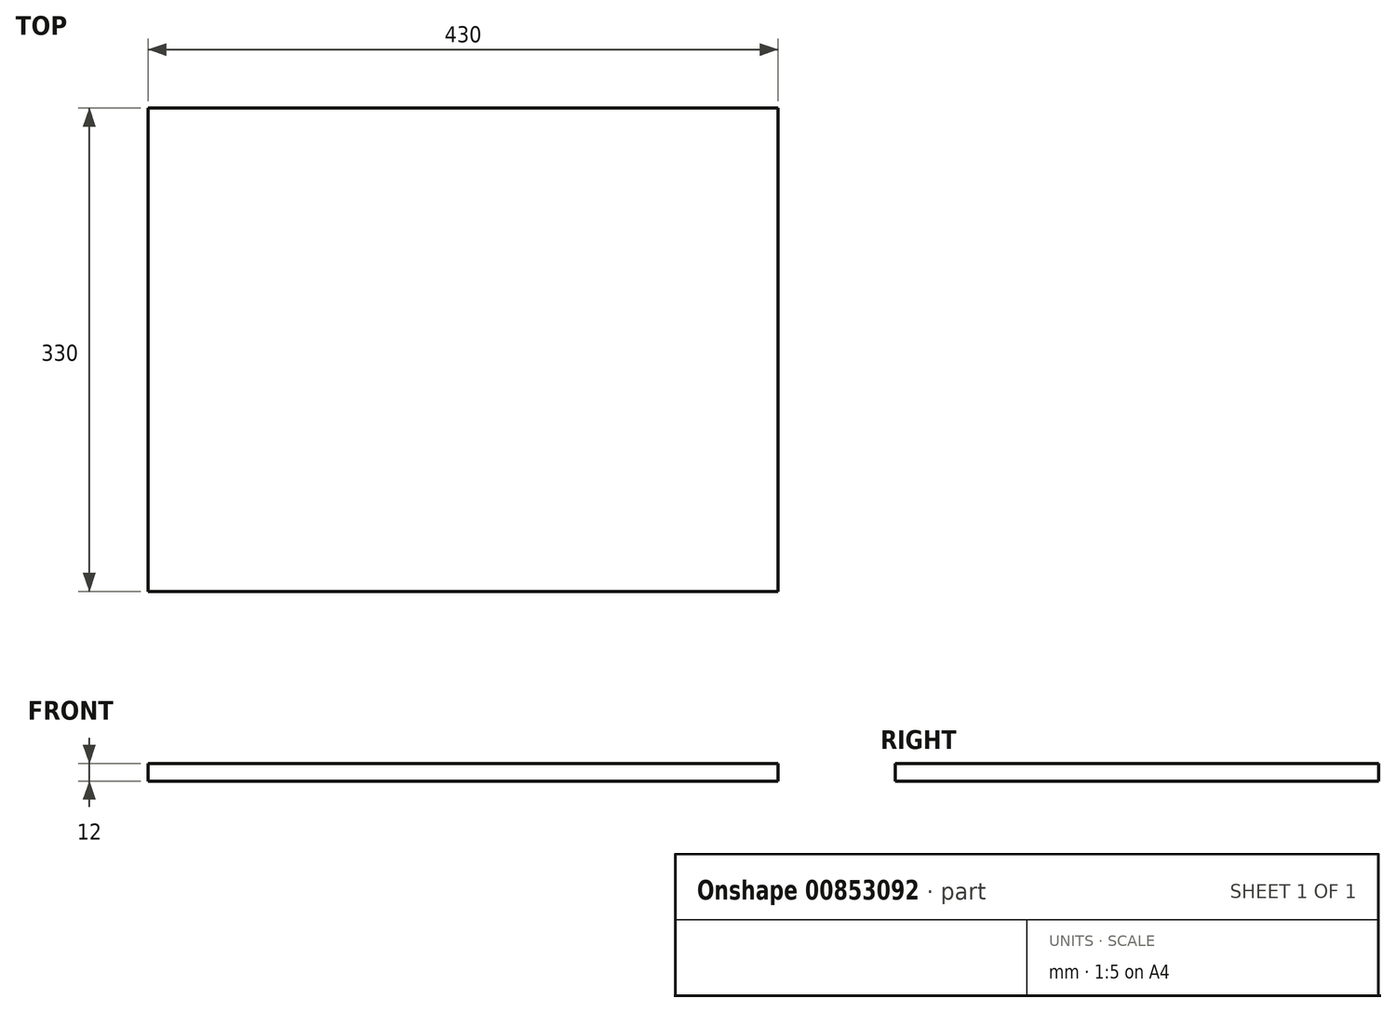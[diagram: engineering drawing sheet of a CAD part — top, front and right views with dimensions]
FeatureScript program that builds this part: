
annotation { "Feature Type Name" : "Feature", "Feature Type Description" : "" }
export const myFeature = defineFeature(function(context is Context, id is Id, definition is map)
    precondition{}
    {
        {
            var Q0;
            Q0=qCreatedBy(makeId("Top.planeOp"),FACE);
            var sketch = newSketch(context, id + "F0", { "sketchPlane" : qUnion([Q0])});
            skLineSegment(sketch, "E0.bottom", {"start": v(215, -165) * mm, "end": v(-215, -165) * mm});
            skLineSegment(sketch, "E0.top", {"start": v(215, 165) * mm, "end": v(-215, 165) * mm});
            skLineSegment(sketch, "E0.left", {"start": v(215, -165) * mm, "end": v(215, 165) * mm});
            skLineSegment(sketch, "E0.right", {"start": v(-215, -165) * mm, "end": v(-215, 165) * mm});
            skPoint(sketch, "E0.middle", {"position": v(0, 0) * mm});
            skSolve(sketch);
        }
        {
            var Q0;
            Q0=makeQuery(id+"F0.imprint","IMPRINT",FACE,{"disambiguationData":[TD([[makeQuery(id+"F0.imprint","IMPRINT",EDGE,{"derivedFrom":sQuery(id+"F0.wireOp",EDGE,"E0.bottom")}),-1.0]])]});
            extrude(context, id + "F1", {"entities" : qUnion([Q0]), "depth" : 6 * mm, "offsetDistance" : 25 * mm, "hasSecondDirection" : true, "secondDirectionOppositeDirection" : true, "secondDirectionDepth" : 6 * mm});
        }
    });
